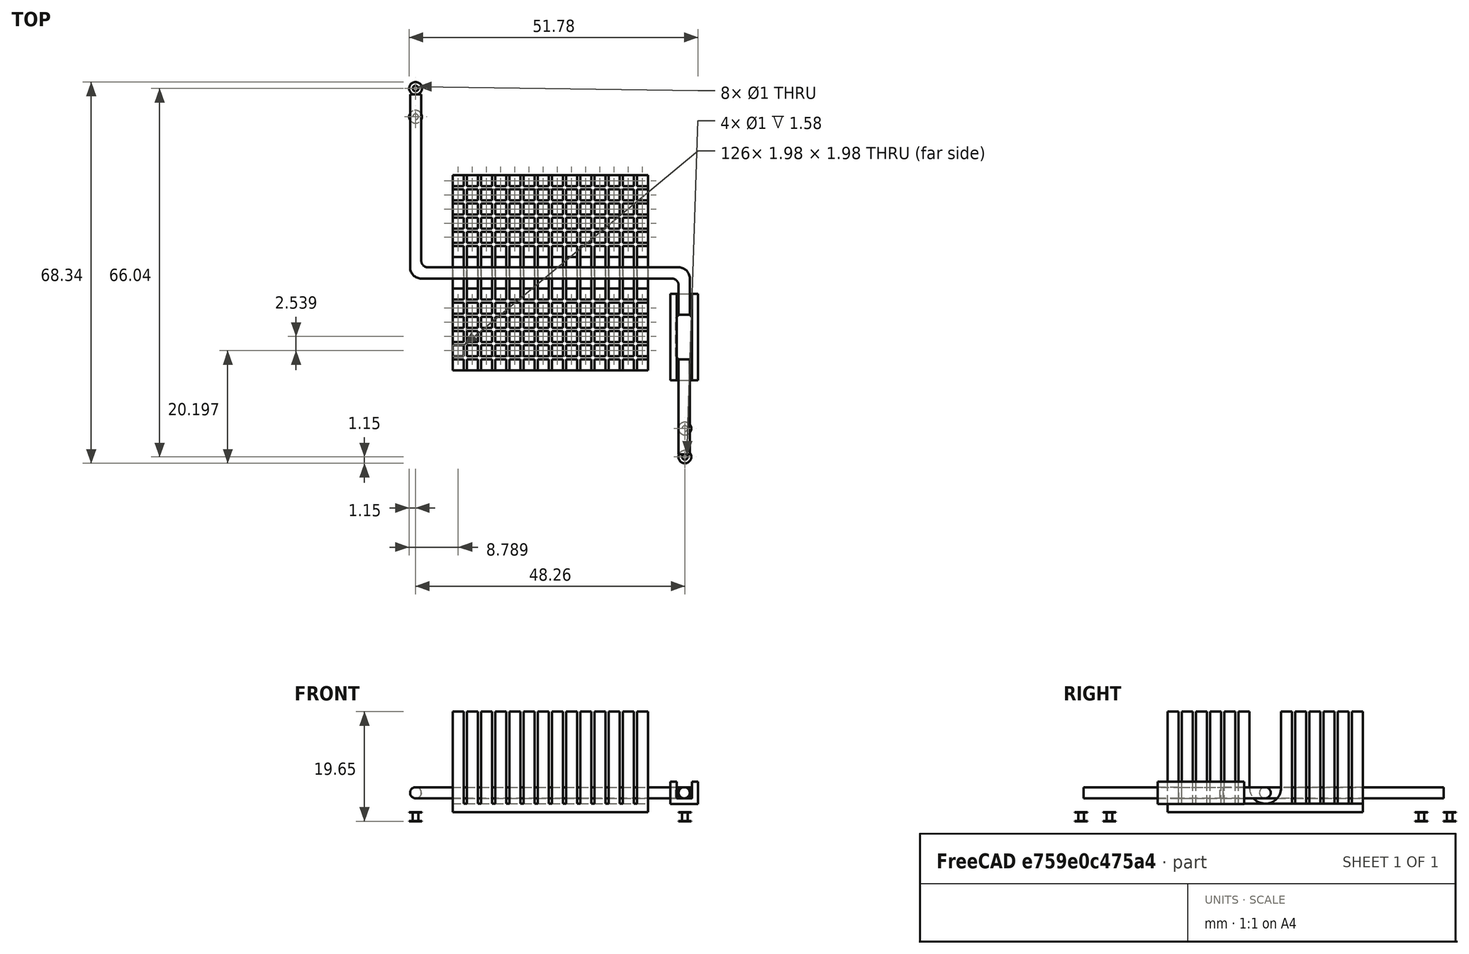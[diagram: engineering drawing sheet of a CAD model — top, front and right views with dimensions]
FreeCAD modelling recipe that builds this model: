
FCSTD DOCUMENT  (FreeCAD 0.20R29177 (Git))
Label: Aavid-heatsink3
License: All rights reserved
LicenseURL: http://en.wikipedia.org/wiki/All_rights_reserved
objects: PartDesign::AdditiveBox×7, PartDesign::Fillet×4, PartDesign::Body×4, Part::FeaturePython×3, Part::Feature×2, Sketcher::SketchObject×2, PartDesign::Chamfer×2, App::DocumentObjectGroup×1, PartDesign::SubtractiveBox×1, Part::Part2DObjectPython×1, PartDesign::Pad×1, App::Part×1
note: 41 computed .brp shape members not serialized (recipe doc carries the construction recipe); baked Part::Feature solids carry a one-line shape summary decoded from their .brp

FEATURE [Part::FeaturePython] FFab_lines  label="FFab"  # a2plus imported part (geometry in sourceFile) (typed FeaturePython)
  fixedPosition = true
FEATURE [Part::FeaturePython] THPs  label="PTHs"  # a2plus imported part (geometry in sourceFile) (typed FeaturePython)
  fixedPosition = true
FEATURE [Part::Feature] Shape001003  label="TopPads"
  shape: bbox 50.56 x 68.34 x 0.01 mm, 16 faces, 4 solids (baked)
FEATURE [Part::Feature] Shape001004  label="BotPads"
  shape: bbox 50.56 x 68.34 x 0.01 mm, 16 faces, 4 solids (baked)
FEATURE [App::DocumentObjectGroup] Heatsink_35x35mm_SpringFixation_fp
  Group = -> [FFab_lines,Shape001003,Shape001004,THPs]
FEATURE [Sketcher::SketchObject] Sketch  label="Pads_Poly"
  FullyConstrained = false
  MapMode = 5
  Support = -> [XY_Plane]
  sketch-geometry (56):
    g0: LineSegment StartX=-17.5 StartY=-17.45 StartZ=0 EndX=-17.5 EndY=17.55 EndZ=0
    g1: LineSegment StartX=-17.5 StartY=17.55 StartZ=0 EndX=-17.5 EndY=-17.55 EndZ=0
    g2: LineSegment StartX=-17.5 StartY=17.55 StartZ=0 EndX=17.55 EndY=17.5 EndZ=0
    g3: LineSegment StartX=17.55 StartY=17.5 StartZ=0 EndX=-17.5 EndY=17.45 EndZ=0
    g4: LineSegment StartX=17.55 StartY=17.5 StartZ=0 EndX=17.55 EndY=-17.5 EndZ=0
    g5: LineSegment StartX=17.5 StartY=-17.55 StartZ=0 EndX=17.45 EndY=17.5 EndZ=0
    g6: LineSegment StartX=17.5 StartY=-17.55 StartZ=0 EndX=-17.5 EndY=-17.55 EndZ=0
    g7: LineSegment StartX=-17.5 StartY=-17.45 StartZ=0 EndX=17.55 EndY=-17.5 EndZ=0
    g8: LineSegment StartX=-26.72 StartY=25.4 StartZ=0 EndX=-26.67 EndY=35.61 EndZ=0
    g9: LineSegment StartX=-26.67 StartY=35.61 StartZ=0 EndX=-26.62 EndY=25.4 EndZ=0
    g10: LineSegment StartX=-21.54 StartY=35.56 StartZ=0 EndX=-21.54 EndY=25.4 EndZ=0
    g11: LineSegment StartX=-21.64 StartY=25.4 StartZ=0 EndX=-21.64 EndY=35.56 EndZ=0
    g12: LineSegment StartX=-21.54 StartY=25.4 StartZ=0 EndX=-26.72 EndY=25.4 EndZ=0
    g13: LineSegment StartX=-26.72 StartY=25.4 StartZ=0 EndX=-21.54 EndY=25.4 EndZ=0
    g14: LineSegment StartX=-22.81 StartY=25.4 StartZ=0 EndX=-22.8271 EndY=2.54 EndZ=0
    g15: ArcOfCircle CenterX=-21.59 CenterY=2.55711 CenterZ=0 NormalX=0 NormalY=0 NormalZ=1 AngleXU=-1.5708 Radius=1.23726 StartAngle=4.72622 EndAngle=6.28319
    g16: LineSegment StartX=-21.59 StartY=1.31985 StartZ=0 EndX=-17.5 EndY=1.32 EndZ=0
    g17: LineSegment StartX=-17.5 StartY=1.22 StartZ=0 EndX=-21.59 EndY=1.29434 EndZ=0
    g18: ArcOfCircle CenterX=-21.5814 CenterY=2.54 CenterZ=0 NormalX=0 NormalY=0 NormalZ=1 AngleXU=-1.5708 Radius=1.24569 StartAngle=4.71239 EndAngle=6.27632
    g19: LineSegment StartX=-22.91 StartY=2.54 StartZ=0 EndX=-22.91 EndY=25.4 EndZ=0
    g20: LineSegment StartX=-25.35 StartY=1.27 StartZ=0 EndX=-25.45 EndY=25.4 EndZ=0
    g21: LineSegment StartX=-25.35 StartY=25.4 StartZ=0 EndX=-25.35 EndY=1.27 EndZ=0
    g22: ArcOfCircle CenterX=-22.86 CenterY=1.26185 CenterZ=0 NormalX=0 NormalY=0 NormalZ=1 AngleXU=-1.5708 Radius=2.49001 StartAngle=4.70911 EndAngle=6.28319
    g23: LineSegment StartX=-22.86 StartY=-1.22817 StartZ=0 EndX=-17.5 EndY=-1.22 EndZ=0
    g24: LineSegment StartX=-17.5 StartY=-1.32 StartZ=0 EndX=-22.86 EndY=-1.32 EndZ=0
    g25: ArcOfCircle CenterX=-22.86 CenterY=1.36352 CenterZ=0 NormalX=0 NormalY=0 NormalZ=1 AngleXU=-1.5708 Radius=2.59169 StartAngle=4.74848 EndAngle=6.28319
    g26: LineSegment StartX=-21.54 StartY=35.56 StartZ=0 EndX=-26.67 EndY=35.61 EndZ=0
    g27: LineSegment StartX=-26.67 StartY=35.61 StartZ=0 EndX=-21.54 EndY=35.56 EndZ=0
    g28: LineSegment StartX=21.59 StartY=-35.51 StartZ=0 EndX=21.59 EndY=-25.25 EndZ=0
    g29: LineSegment StartX=21.59 StartY=-25.25 StartZ=0 EndX=21.59 EndY=-35.51 EndZ=0
    g30: LineSegment StartX=26.67 StartY=-25.25 StartZ=0 EndX=26.72 EndY=-35.46 EndZ=0
    g31: LineSegment StartX=26.62 StartY=-35.46 StartZ=0 EndX=26.67 EndY=-25.25 EndZ=0
    g32: LineSegment StartX=21.59 StartY=-25.25 StartZ=0 EndX=26.67 EndY=-25.25 EndZ=0
    g33: LineSegment StartX=26.67 StartY=-25.35 StartZ=0 EndX=21.59 EndY=-25.35 EndZ=0
    g34: LineSegment StartX=25.35 StartY=-25.3 StartZ=0 EndX=25.35 EndY=-1.17 EndZ=0
    g35: ArcOfCircle CenterX=22.797 CenterY=-1.16077 CenterZ=0 NormalX=0 NormalY=0 NormalZ=1 AngleXU=1.5708 Radius=2.57229 StartAngle=4.7088 EndAngle=6.25869
    g36: LineSegment StartX=22.86 StartY=1.32 StartZ=0 EndX=17.5 EndY=1.32 EndZ=0
    g37: LineSegment StartX=17.5 StartY=1.42 StartZ=0 EndX=22.86 EndY=1.41075 EndZ=0
    g38: ArcOfCircle CenterX=22.86 CenterY=-1.17 CenterZ=0 NormalX=0 NormalY=0 NormalZ=1 AngleXU=1.5708 Radius=2.58075 StartAngle=4.71239 EndAngle=6.28319
    g39: LineSegment StartX=25.4407 StartY=-1.17 StartZ=0 EndX=25.45 EndY=-25.3 EndZ=0
    g40: LineSegment StartX=21.59 StartY=-35.51 StartZ=0 EndX=26.72 EndY=-35.46 EndZ=0
    g41: LineSegment StartX=26.72 StartY=-35.46 StartZ=0 EndX=21.59 EndY=-35.51 EndZ=0
    g42: LineSegment StartX=22.81 StartY=-2.44 StartZ=0 EndX=22.91 EndY=-25.3 EndZ=0
    g43: LineSegment StartX=22.81 StartY=-25.3 StartZ=0 EndX=22.81 EndY=-2.44 EndZ=0
    g44: ArcOfCircle CenterX=21.59 CenterY=-2.35008 CenterZ=0 NormalX=0 NormalY=0 NormalZ=1 AngleXU=1.5708 Radius=1.22331 StartAngle=4.63882 EndAngle=6.28319
    g45: LineSegment StartX=21.59 StartY=-1.12677 StartZ=0 EndX=17.5 EndY=-1.22 EndZ=0
    g46: LineSegment StartX=17.5 StartY=-1.12 StartZ=0 EndX=21.59 EndY=-1.12677 EndZ=0
    g47: ArcOfCircle CenterX=21.59 CenterY=-2.44679 CenterZ=0 NormalX=0 NormalY=0 NormalZ=1 AngleXU=1.5708 Radius=1.32002 StartAngle=4.71753 EndAngle=6.28319
    g48: LineSegment StartX=21.59 StartY=-18.525 StartZ=0 EndX=21.59 EndY=-3.125 EndZ=0
    g49: LineSegment StartX=21.59 StartY=-3.125 StartZ=0 EndX=21.59 EndY=-18.525 EndZ=0
    g50: LineSegment StartX=21.59 StartY=-18.525 StartZ=0 EndX=26.67 EndY=-18.525 EndZ=0
    g51: LineSegment StartX=26.67 StartY=-18.625 StartZ=0 EndX=21.59 EndY=-18.625 EndZ=0
    g52: LineSegment StartX=26.67 StartY=-18.525 StartZ=0 EndX=26.62 EndY=-3.075 EndZ=0
    g53: LineSegment StartX=26.72 StartY=-3.075 StartZ=0 EndX=26.67 EndY=-18.525 EndZ=0
    g54: LineSegment StartX=21.59 StartY=-3.125 StartZ=0 EndX=26.72 EndY=-3.075 EndZ=0
    g55: LineSegment StartX=26.72 StartY=-3.075 StartZ=0 EndX=21.59 EndY=-3.125 EndZ=0
  constraints (50):
    c: Coincident(g8,g12)
    c: Coincident(g8,g13)
    c: Coincident(g27,g8)
    c: Coincident(g27,g9)
    c: Coincident(g27,g26)
    c: Coincident(g22,g20)
    c: Coincident(g23,g25)
    c: Coincident(g23,g22)
    c: Coincident(g14,g15)
    c: Coincident(g14,g18)
    c: Coincident(g18,g17)
    c: Coincident(g15,g16)
    c: Coincident(g10,g12)
    c: Coincident(g10,g13)
    c: Coincident(g10,g26)
    c: Coincident(g10,g27)
    c: Coincident(g6,g1)
    c: Coincident(g7,g0)
    c: Coincident(g2,g0)
    c: Coincident(g2,g1)
    c: Coincident(g6,g5)
    c: Coincident(g4,g7)
    c: Coincident(g4,g3)
    c: Coincident(g4,g2)
    c: Coincident(g41,g28)
    c: Coincident(g41,g40)
    c: Coincident(g41,g29)
    c: Coincident(g32,g28)
    c: Coincident(g32,g29)
    c: Coincident(g50,g48)
    c: Coincident(g50,g49)
    c: Coincident(g55,g54)
    c: Coincident(g55,g48)
    c: Coincident(g55,g49)
    c: Coincident(g47,g45)
    c: Coincident(g47,g44)
    c: Coincident(g47,g46)
    c: Coincident(g44,g43)
    c: Coincident(g44,g42)
    c: Coincident(g37,g35)
    c: Coincident(g37,g38)
    c: Coincident(g39,g38)
    c: Coincident(g30,g40)
    c: Coincident(g30,g41)
    c: Coincident(g32,g31)
    c: Coincident(g32,g30)
    c: Coincident(g50,g52)
    c: Coincident(g50,g53)
    c: Coincident(g53,g54)
    c: Coincident(g53,g55)
FEATURE [PartDesign::AdditiveBox] Box  label="metal"
  AttacherType = Attacher::AttachEngine3D
  AttachmentOffset = pos=(-17.5,-17.5,0) rot=(0,0,1;0rad)
  Height = 1.5
  Length = 35
  MapMode = 5
  Placement = pos=(-17.5,-17.5,0) rot=(0,0,1;0rad)
  Support = -> [XY_Plane]
  Width = 35
FEATURE [PartDesign::AdditiveBox] Box010  label="base-lower-arm"
  AttacherType = Attacher::AttachEngine3D
  AttachmentOffset = pos=(23,-32,2.5) rot=(0,0,1;0rad)
  Height = 2
  Length = 2
  MapMode = 5
  Placement = pos=(23,-32,2.5) rot=(0,0,1;0rad)
  Support = -> [XY_Plane001]
  Width = 33.5
FEATURE [PartDesign::AdditiveBox] Box011  label="mid-arm"
  AttacherType = Attacher::AttachEngine3D
  AttachmentOffset = pos=(-23.1,-0.5,2.5) rot=(0,0,1;0rad)
  BaseFeature = -> Box010
  Height = 2
  Length = 46.1
  MapMode = 5
  Placement = pos=(-23.1,-0.5,2.5) rot=(0,0,1;0rad)
  Support = -> [XY_Plane001]
  Width = 2
FEATURE [PartDesign::AdditiveBox] Box012
  AttacherType = Attacher::AttachEngine3D
  AttachmentOffset = pos=(-25.1,-0.5,2.5) rot=(0,0,1;0rad)
  BaseFeature = -> Box011
  Height = 2
  Length = 2
  MapMode = 5
  Placement = pos=(-25.1,-0.5,2.5) rot=(0,0,1;0rad)
  Support = -> [XY_Plane001]
  Width = 33
FEATURE [PartDesign::Fillet] Fillet  label="outer-bend"
  Base = -> Box012 [Edge25,Edge19]
  BaseFeature = -> Box012
  Placement = pos=(-25.1,-0.5,2.5) rot=(0,0,1;0rad)
  Radius = 1.99
  SupportTransform = false
  UseAllEdges = false
FEATURE [PartDesign::Fillet] Fillet001  label="inner-bend"
  Base = -> Fillet [Edge17,Edge23]
  BaseFeature = -> Fillet
  Placement = pos=(-25.1,-0.5,2.5) rot=(0,0,1;0rad)
  Radius = 1.2
  SupportTransform = false
  UseAllEdges = false
FEATURE [PartDesign::Fillet] Fillet002  label="outer-smooth"
  Base = -> Fillet001 [Edge7,Edge5,Edge11,Edge12,Edge33,Edge20,Edge24,Edge29,Edge38,Edge25,Edge10,Edge50,Edge47,Edge43,Edge31,Edge1,Edge15,Edge16,Edge37,Edge35,Edge36]
  BaseFeature = -> Fillet001
  Placement = pos=(-25.1,-0.5,2.5) rot=(0,0,1;0rad)
  Radius = 0.99
  SupportTransform = false
  UseAllEdges = false
FEATURE [PartDesign::AdditiveBox] Box014
  AttacherType = Attacher::AttachEngine3D
  AttachmentOffset = pos=(21.5,-18.6,1.5) rot=(0,0,1;0rad)
  Height = 4
  Length = 5
  MapMode = 5
  Placement = pos=(21.5,-18.6,1.5) rot=(0,0,1;0rad)
  Support = -> [XY_Plane002]
  Width = 15.5
FEATURE [PartDesign::SubtractiveBox] Box015
  AttacherType = Attacher::AttachEngine3D
  AttachmentOffset = pos=(22.65,-19,2.5) rot=(0,0,1;0rad)
  BaseFeature = -> Box014
  Height = 3
  Length = 2.75
  MapMode = 5
  Placement = pos=(22.65,-19,2.5) rot=(0,0,1;0rad)
  Support = -> [XY_Plane002]
  Width = 16
FEATURE [PartDesign::AdditiveBox] Box016
  AttacherType = Attacher::AttachEngine3D
  AttachmentOffset = pos=(-15,-15,0) rot=(0,0,1;0rad)
  Height = 0.05
  Length = 30
  MapMode = 5
  Placement = pos=(-15,-15,0) rot=(0,0,1;0rad)
  Support = -> [XY_Plane004]
  Width = 30
FEATURE [Part::Part2DObjectPython] Shape2DView  # Draft 2D object (typed FeaturePython)
  AutoUpdate = true
  Clip = false
  FuseArch = false
  HiddenLines = false
  InPlace = true
  OnlySolids = false
  Projection = (0,0,1)
  ProjectionMode = 0
  SegmentLength = 0.05
  Tessellation = false
  VisibleOnly = false
FEATURE [Part::FeaturePython] Array  # Draft array (typed FeaturePython)
  AlwaysSyncPlacement = false
  Angle = 360
  ArrayType = 0
  Axis = (0,0,1)
  Base = -> Shape2DView
  Center = (0,0,0)
  Count = 196
  ExpandArray = false
  Fuse = false
  IntervalAxis = (0,0,0)
  IntervalX = (2.5387,0,0)
  IntervalY = (0,2.5387,0)
  IntervalZ = (0,0,100)
  NumberCircles = 3
  NumberPolar = 5
  NumberX = 14
  NumberY = 14
  NumberZ = 1
  Placement = pos=(0,-33.0245,0) rot=(0,0,1;0rad)
  PlacementList = 196 placements: [(0,0,0),(0,2.5387,0),(0,5.0774,0),(0,7.6161,0),(0,10.1548,0),(0,12.6935,0),(0,15.2322,0),(0,17.7709,0),(0,20.3096,0),(0,22.8483,0),(0,25.387,0),(0,27.9257,0),(0,30.4644,0),(0,33.0031,0),(2.5387,0,0),(2.5387,2.5387,0),(2.5387,5.0774,0),(2.5387,7.6161,0),(2.5387,10.1548,0),(2.5387,12.6935,0),(2.5387,15.2322,0),(2.5387,17.7709,0),(2.5387,20.3096,0),(2.5387,22.8483,0),(2.5387,25.387,0),+171 more]
  RadialDistance = 50
  ScaleList = (196) [(1,1,1),(1,1,1),(1,1,1),(1,1,1),(1,1,1),(1,1,1),(1,1,1),(1,1,1),(1,1,1),(1,1,1),(1,1,1),(1,1,1),(1,1,1),(1,1,1),(1,1,1),(1,1,1),(1,1,1),(1,1,1),+178 more]
  Symmetry = 1
  TangentialDistance = 25
FEATURE [Sketcher::SketchObject] Sketch001  label="fin-sketch"
  FullyConstrained = false
  sketch-geometry (672):
    g0: LineSegment StartX=-17.5 StartY=-17.5 StartZ=0 EndX=-17.5 EndY=-15.5245 EndZ=0
    g1: LineSegment StartX=-15.5245 StartY=-17.5 StartZ=0 EndX=-15.5245 EndY=-15.5245 EndZ=0
    g2: LineSegment StartX=-17.5 StartY=-17.5 StartZ=0 EndX=-15.5245 EndY=-17.5 EndZ=0
    g3: LineSegment StartX=-17.5 StartY=-15.5245 StartZ=0 EndX=-15.5245 EndY=-15.5245 EndZ=0
    g4: LineSegment StartX=-17.5 StartY=-14.9613 StartZ=0 EndX=-17.5 EndY=-12.9858 EndZ=0
    g5: LineSegment StartX=-15.5245 StartY=-14.9613 StartZ=0 EndX=-15.5245 EndY=-12.9858 EndZ=0
    g6: LineSegment StartX=-17.5 StartY=-14.9613 StartZ=0 EndX=-15.5245 EndY=-14.9613 EndZ=0
    g7: LineSegment StartX=-17.5 StartY=-12.9858 StartZ=0 EndX=-15.5245 EndY=-12.9858 EndZ=0
    g8: LineSegment StartX=-17.5 StartY=-12.4226 StartZ=0 EndX=-17.5 EndY=-10.4471 EndZ=0
    g9: LineSegment StartX=-15.5245 StartY=-12.4226 StartZ=0 EndX=-15.5245 EndY=-10.4471 EndZ=0
    g10: LineSegment StartX=-17.5 StartY=-12.4226 StartZ=0 EndX=-15.5245 EndY=-12.4226 EndZ=0
    g11: LineSegment StartX=-17.5 StartY=-10.4471 StartZ=0 EndX=-15.5245 EndY=-10.4471 EndZ=0
    g12: LineSegment StartX=-17.5 StartY=-9.88385 StartZ=0 EndX=-17.5 EndY=-7.90835 EndZ=0
    g13: LineSegment StartX=-15.5245 StartY=-9.88385 StartZ=0 EndX=-15.5245 EndY=-7.90835 EndZ=0
    g14: LineSegment StartX=-17.5 StartY=-9.88385 StartZ=0 EndX=-15.5245 EndY=-9.88385 EndZ=0
    g15: LineSegment StartX=-17.5 StartY=-7.90835 StartZ=0 EndX=-15.5245 EndY=-7.90835 EndZ=0
    g16: LineSegment StartX=-17.5 StartY=-7.34515 StartZ=0 EndX=-17.5 EndY=-5.36965 EndZ=0
    g17: LineSegment StartX=-15.5245 StartY=-7.34515 StartZ=0 EndX=-15.5245 EndY=-5.36965 EndZ=0
    g18: LineSegment StartX=-17.5 StartY=-7.34515 StartZ=0 EndX=-15.5245 EndY=-7.34515 EndZ=0
    g19: LineSegment StartX=-17.5 StartY=-5.36965 StartZ=0 EndX=-15.5245 EndY=-5.36965 EndZ=0
    g20: LineSegment StartX=-17.5 StartY=-4.80645 StartZ=0 EndX=-17.5 EndY=-2.83095 EndZ=0
    g21: LineSegment StartX=-15.5245 StartY=-4.80645 StartZ=0 EndX=-15.5245 EndY=-2.83095 EndZ=0
    g22: LineSegment StartX=-17.5 StartY=-4.80645 StartZ=0 EndX=-15.5245 EndY=-4.80645 EndZ=0
    g23: LineSegment StartX=-17.5 StartY=-2.83095 StartZ=0 EndX=-15.5245 EndY=-2.83095 EndZ=0
    g24: LineSegment StartX=-17.5 StartY=-2.26775 StartZ=0 EndX=-17.5 EndY=-0.292254 EndZ=0
    g25: LineSegment StartX=-15.5245 StartY=-2.26775 StartZ=0 EndX=-15.5245 EndY=-0.292254 EndZ=0
    g26: LineSegment StartX=-17.5 StartY=-2.26775 StartZ=0 EndX=-15.5245 EndY=-2.26775 EndZ=0
    g27: LineSegment StartX=-17.5 StartY=-0.292254 StartZ=0 EndX=-15.5245 EndY=-0.292254 EndZ=0
    g28: LineSegment StartX=-17.5 StartY=0.270946 StartZ=0 EndX=-17.5 EndY=2.24645 EndZ=0
    g29: LineSegment StartX=-15.5245 StartY=0.270946 StartZ=0 EndX=-15.5245 EndY=2.24645 EndZ=0
    g30: LineSegment StartX=-17.5 StartY=0.270946 StartZ=0 EndX=-15.5245 EndY=0.270946 EndZ=0
    g31: LineSegment StartX=-17.5 StartY=2.24645 StartZ=0 EndX=-15.5245 EndY=2.24645 EndZ=0
    g32: LineSegment StartX=-17.5 StartY=2.80965 StartZ=0 EndX=-17.5 EndY=4.78515 EndZ=0
    g33: LineSegment StartX=-15.5245 StartY=2.80965 StartZ=0 EndX=-15.5245 EndY=4.78515 EndZ=0
    g34: LineSegment StartX=-17.5 StartY=2.80965 StartZ=0 EndX=-15.5245 EndY=2.80965 EndZ=0
    g35: LineSegment StartX=-17.5 StartY=4.78515 StartZ=0 EndX=-15.5245 EndY=4.78515 EndZ=0
    g36: LineSegment StartX=-17.5 StartY=5.34835 StartZ=0 EndX=-17.5 EndY=7.32385 EndZ=0
    g37: LineSegment StartX=-15.5245 StartY=5.34835 StartZ=0 EndX=-15.5245 EndY=7.32385 EndZ=0
    g38: LineSegment StartX=-17.5 StartY=5.34835 StartZ=0 EndX=-15.5245 EndY=5.34835 EndZ=0
    g39: LineSegment StartX=-17.5 StartY=7.32385 StartZ=0 EndX=-15.5245 EndY=7.32385 EndZ=0
    g40: LineSegment StartX=-17.5 StartY=7.88705 StartZ=0 EndX=-17.5 EndY=9.86255 EndZ=0
    g41: LineSegment StartX=-15.5245 StartY=7.88705 StartZ=0 EndX=-15.5245 EndY=9.86255 EndZ=0
    g42: LineSegment StartX=-17.5 StartY=7.88705 StartZ=0 EndX=-15.5245 EndY=7.88705 EndZ=0
    g43: LineSegment StartX=-17.5 StartY=9.86255 StartZ=0 EndX=-15.5245 EndY=9.86255 EndZ=0
    g44: LineSegment StartX=-17.5 StartY=10.4257 StartZ=0 EndX=-17.5 EndY=12.4012 EndZ=0
    g45: LineSegment StartX=-15.5245 StartY=10.4257 StartZ=0 EndX=-15.5245 EndY=12.4012 EndZ=0
    g46: LineSegment StartX=-17.5 StartY=10.4257 StartZ=0 EndX=-15.5245 EndY=10.4257 EndZ=0
    g47: LineSegment StartX=-17.5 StartY=12.4012 StartZ=0 EndX=-15.5245 EndY=12.4012 EndZ=0
    g48: LineSegment StartX=-17.5 StartY=12.9644 StartZ=0 EndX=-17.5 EndY=14.9399 EndZ=0
    g49: LineSegment StartX=-15.5245 StartY=12.9644 StartZ=0 EndX=-15.5245 EndY=14.9399 EndZ=0
    g50: LineSegment StartX=-17.5 StartY=12.9644 StartZ=0 EndX=-15.5245 EndY=12.9644 EndZ=0
    g51: LineSegment StartX=-17.5 StartY=14.9399 StartZ=0 EndX=-15.5245 EndY=14.9399 EndZ=0
    g52: LineSegment StartX=-17.5 StartY=15.5031 StartZ=0 EndX=-17.5 EndY=17.4786 EndZ=0
    g53: LineSegment StartX=-15.5245 StartY=15.5031 StartZ=0 EndX=-15.5245 EndY=17.4786 EndZ=0
    g54: LineSegment StartX=-17.5 StartY=15.5031 StartZ=0 EndX=-15.5245 EndY=15.5031 EndZ=0
    g55: LineSegment StartX=-17.5 StartY=17.4786 StartZ=0 EndX=-15.5245 EndY=17.4786 EndZ=0
    g56: LineSegment StartX=-14.9613 StartY=-17.5 StartZ=0 EndX=-14.9613 EndY=-15.5245 EndZ=0
    g57: LineSegment StartX=-12.9858 StartY=-17.5 StartZ=0 EndX=-12.9858 EndY=-15.5245 EndZ=0
    g58: LineSegment StartX=-14.9613 StartY=-17.5 StartZ=0 EndX=-12.9858 EndY=-17.5 EndZ=0
    g59: LineSegment StartX=-14.9613 StartY=-15.5245 StartZ=0 EndX=-12.9858 EndY=-15.5245 EndZ=0
    g60: LineSegment StartX=-14.9613 StartY=-14.9613 StartZ=0 EndX=-14.9613 EndY=-12.9858 EndZ=0
    g61: LineSegment StartX=-12.9858 StartY=-14.9613 StartZ=0 EndX=-12.9858 EndY=-12.9858 EndZ=0
    g62: LineSegment StartX=-14.9613 StartY=-14.9613 StartZ=0 EndX=-12.9858 EndY=-14.9613 EndZ=0
    g63: LineSegment StartX=-14.9613 StartY=-12.9858 StartZ=0 EndX=-12.9858 EndY=-12.9858 EndZ=0
    g64: LineSegment StartX=-14.9613 StartY=-12.4226 StartZ=0 EndX=-14.9613 EndY=-10.4471 EndZ=0
    g65: LineSegment StartX=-12.9858 StartY=-12.4226 StartZ=0 EndX=-12.9858 EndY=-10.4471 EndZ=0
    g66: LineSegment StartX=-14.9613 StartY=-12.4226 StartZ=0 EndX=-12.9858 EndY=-12.4226 EndZ=0
    g67: LineSegment StartX=-14.9613 StartY=-10.4471 StartZ=0 EndX=-12.9858 EndY=-10.4471 EndZ=0
    g68: LineSegment StartX=-14.9613 StartY=-9.88385 StartZ=0 EndX=-14.9613 EndY=-7.90835 EndZ=0
    g69: LineSegment StartX=-12.9858 StartY=-9.88385 StartZ=0 EndX=-12.9858 EndY=-7.90835 EndZ=0
    g70: LineSegment StartX=-14.9613 StartY=-9.88385 StartZ=0 EndX=-12.9858 EndY=-9.88385 EndZ=0
    g71: LineSegment StartX=-14.9613 StartY=-7.90835 StartZ=0 EndX=-12.9858 EndY=-7.90835 EndZ=0
    g72: LineSegment StartX=-14.9613 StartY=-7.34515 StartZ=0 EndX=-14.9613 EndY=-5.36965 EndZ=0
    g73: LineSegment StartX=-12.9858 StartY=-7.34515 StartZ=0 EndX=-12.9858 EndY=-5.36965 EndZ=0
    g74: LineSegment StartX=-14.9613 StartY=-7.34515 StartZ=0 EndX=-12.9858 EndY=-7.34515 EndZ=0
    g75: LineSegment StartX=-14.9613 StartY=-5.36965 StartZ=0 EndX=-12.9858 EndY=-5.36965 EndZ=0
    g76: LineSegment StartX=-14.9613 StartY=-4.80645 StartZ=0 EndX=-14.9613 EndY=-2.83095 EndZ=0
    g77: LineSegment StartX=-12.9858 StartY=-4.80645 StartZ=0 EndX=-12.9858 EndY=-2.83095 EndZ=0
    g78: LineSegment StartX=-14.9613 StartY=-4.80645 StartZ=0 EndX=-12.9858 EndY=-4.80645 EndZ=0
    g79: LineSegment StartX=-14.9613 StartY=-2.83095 StartZ=0 EndX=-12.9858 EndY=-2.83095 EndZ=0
    g80: LineSegment StartX=-14.9613 StartY=-2.26775 StartZ=0 EndX=-14.9613 EndY=-0.292254 EndZ=0
    g81: LineSegment StartX=-12.9858 StartY=-2.26775 StartZ=0 EndX=-12.9858 EndY=-0.292254 EndZ=0
    g82: LineSegment StartX=-14.9613 StartY=-2.26775 StartZ=0 EndX=-12.9858 EndY=-2.26775 EndZ=0
    g83: LineSegment StartX=-14.9613 StartY=-0.292254 StartZ=0 EndX=-12.9858 EndY=-0.292254 EndZ=0
    g84: LineSegment StartX=-14.9613 StartY=0.270946 StartZ=0 EndX=-14.9613 EndY=2.24645 EndZ=0
    g85: LineSegment StartX=-12.9858 StartY=0.270946 StartZ=0 EndX=-12.9858 EndY=2.24645 EndZ=0
    g86: LineSegment StartX=-14.9613 StartY=0.270946 StartZ=0 EndX=-12.9858 EndY=0.270946 EndZ=0
    g87: LineSegment StartX=-14.9613 StartY=2.24645 StartZ=0 EndX=-12.9858 EndY=2.24645 EndZ=0
    g88: LineSegment StartX=-14.9613 StartY=2.80965 StartZ=0 EndX=-14.9613 EndY=4.78515 EndZ=0
    g89: LineSegment StartX=-12.9858 StartY=2.80965 StartZ=0 EndX=-12.9858 EndY=4.78515 EndZ=0
    g90: LineSegment StartX=-14.9613 StartY=2.80965 StartZ=0 EndX=-12.9858 EndY=2.80965 EndZ=0
    g91: LineSegment StartX=-14.9613 StartY=4.78515 StartZ=0 EndX=-12.9858 EndY=4.78515 EndZ=0
    g92: LineSegment StartX=-14.9613 StartY=5.34835 StartZ=0 EndX=-14.9613 EndY=7.32385 EndZ=0
    g93: LineSegment StartX=-12.9858 StartY=5.34835 StartZ=0 EndX=-12.9858 EndY=7.32385 EndZ=0
    g94: LineSegment StartX=-14.9613 StartY=5.34835 StartZ=0 EndX=-12.9858 EndY=5.34835 EndZ=0
    g95: LineSegment StartX=-14.9613 StartY=7.32385 StartZ=0 EndX=-12.9858 EndY=7.32385 EndZ=0
    g96: LineSegment StartX=-14.9613 StartY=7.88705 StartZ=0 EndX=-14.9613 EndY=9.86255 EndZ=0
    g97: LineSegment StartX=-12.9858 StartY=7.88705 StartZ=0 EndX=-12.9858 EndY=9.86255 EndZ=0
    g98: LineSegment StartX=-14.9613 StartY=7.88705 StartZ=0 EndX=-12.9858 EndY=7.88705 EndZ=0
    g99: LineSegment StartX=-14.9613 StartY=9.86255 StartZ=0 EndX=-12.9858 EndY=9.86255 EndZ=0
    g100: LineSegment StartX=-14.9613 StartY=10.4257 StartZ=0 EndX=-14.9613 EndY=12.4012 EndZ=0
    g101: LineSegment StartX=-12.9858 StartY=10.4257 StartZ=0 EndX=-12.9858 EndY=12.4012 EndZ=0
    g102: LineSegment StartX=-14.9613 StartY=10.4257 StartZ=0 EndX=-12.9858 EndY=10.4257 EndZ=0
    g103: LineSegment StartX=-14.9613 StartY=12.4012 StartZ=0 EndX=-12.9858 EndY=12.4012 EndZ=0
    g104: LineSegment StartX=-14.9613 StartY=12.9644 StartZ=0 EndX=-14.9613 EndY=14.9399 EndZ=0
    g105: LineSegment StartX=-12.9858 StartY=12.9644 StartZ=0 EndX=-12.9858 EndY=14.9399 EndZ=0
    g106: LineSegment StartX=-14.9613 StartY=12.9644 StartZ=0 EndX=-12.9858 EndY=12.9644 EndZ=0
    g107: LineSegment StartX=-14.9613 StartY=14.9399 StartZ=0 EndX=-12.9858 EndY=14.9399 EndZ=0
    g108: LineSegment StartX=-14.9613 StartY=15.5031 StartZ=0 EndX=-14.9613 EndY=17.4786 EndZ=0
    g109: LineSegment StartX=-12.9858 StartY=15.5031 StartZ=0 EndX=-12.9858 EndY=17.4786 EndZ=0
    g110: LineSegment StartX=-14.9613 StartY=15.5031 StartZ=0 EndX=-12.9858 EndY=15.5031 EndZ=0
    g111: LineSegment StartX=-14.9613 StartY=17.4786 StartZ=0 EndX=-12.9858 EndY=17.4786 EndZ=0
    g112: LineSegment StartX=-12.4226 StartY=-17.5 StartZ=0 EndX=-12.4226 EndY=-15.5245 EndZ=0
    g113: LineSegment StartX=-10.4471 StartY=-17.5 StartZ=0 EndX=-10.4471 EndY=-15.5245 EndZ=0
    g114: LineSegment StartX=-12.4226 StartY=-17.5 StartZ=0 EndX=-10.4471 EndY=-17.5 EndZ=0
    g115: LineSegment StartX=-12.4226 StartY=-15.5245 StartZ=0 EndX=-10.4471 EndY=-15.5245 EndZ=0
    g116: LineSegment StartX=-12.4226 StartY=-14.9613 StartZ=0 EndX=-12.4226 EndY=-12.9858 EndZ=0
    g117: LineSegment StartX=-10.4471 StartY=-14.9613 StartZ=0 EndX=-10.4471 EndY=-12.9858 EndZ=0
    g118: LineSegment StartX=-12.4226 StartY=-14.9613 StartZ=0 EndX=-10.4471 EndY=-14.9613 EndZ=0
    g119: LineSegment StartX=-12.4226 StartY=-12.9858 StartZ=0 EndX=-10.4471 EndY=-12.9858 EndZ=0
    g120: LineSegment StartX=-12.4226 StartY=-12.4226 StartZ=0 EndX=-12.4226 EndY=-10.4471 EndZ=0
    g121: LineSegment StartX=-10.4471 StartY=-12.4226 StartZ=0 EndX=-10.4471 EndY=-10.4471 EndZ=0
    g122: LineSegment StartX=-12.4226 StartY=-12.4226 StartZ=0 EndX=-10.4471 EndY=-12.4226 EndZ=0
    g123: LineSegment StartX=-12.4226 StartY=-10.4471 StartZ=0 EndX=-10.4471 EndY=-10.4471 EndZ=0
    g124: LineSegment StartX=-12.4226 StartY=-9.88385 StartZ=0 EndX=-12.4226 EndY=-7.90835 EndZ=0
    g125: LineSegment StartX=-10.4471 StartY=-9.88385 StartZ=0 EndX=-10.4471 EndY=-7.90835 EndZ=0
    g126: LineSegment StartX=-12.4226 StartY=-9.88385 StartZ=0 EndX=-10.4471 EndY=-9.88385 EndZ=0
    g127: LineSegment StartX=-12.4226 StartY=-7.90835 StartZ=0 EndX=-10.4471 EndY=-7.90835 EndZ=0
    g128: LineSegment StartX=-12.4226 StartY=-7.34515 StartZ=0 EndX=-12.4226 EndY=-5.36965 EndZ=0
    g129: LineSegment StartX=-10.4471 StartY=-7.34515 StartZ=0 EndX=-10.4471 EndY=-5.36965 EndZ=0
    g130: LineSegment StartX=-12.4226 StartY=-7.34515 StartZ=0 EndX=-10.4471 EndY=-7.34515 EndZ=0
    g131: LineSegment StartX=-12.4226 StartY=-5.36965 StartZ=0 EndX=-10.4471 EndY=-5.36965 EndZ=0
    g132: LineSegment StartX=-12.4226 StartY=-4.80645 StartZ=0 EndX=-12.4226 EndY=-2.83095 EndZ=0
    g133: LineSegment StartX=-10.4471 StartY=-4.80645 StartZ=0 EndX=-10.4471 EndY=-2.83095 EndZ=0
    g134: LineSegment StartX=-12.4226 StartY=-4.80645 StartZ=0 EndX=-10.4471 EndY=-4.80645 EndZ=0
    g135: LineSegment StartX=-12.4226 StartY=-2.83095 StartZ=0 EndX=-10.4471 EndY=-2.83095 EndZ=0
    g136: LineSegment StartX=-12.4226 StartY=-2.26775 StartZ=0 EndX=-12.4226 EndY=-0.292254 EndZ=0
    g137: LineSegment StartX=-10.4471 StartY=-2.26775 StartZ=0 EndX=-10.4471 EndY=-0.292254 EndZ=0
    g138: LineSegment StartX=-12.4226 StartY=-2.26775 StartZ=0 EndX=-10.4471 EndY=-2.26775 EndZ=0
    g139: LineSegment StartX=-12.4226 StartY=-0.292254 StartZ=0 EndX=-10.4471 EndY=-0.292254 EndZ=0
    g140: LineSegment StartX=-12.4226 StartY=0.270946 StartZ=0 EndX=-12.4226 EndY=2.24645 EndZ=0
    g141: LineSegment StartX=-10.4471 StartY=0.270946 StartZ=0 EndX=-10.4471 EndY=2.24645 EndZ=0
    g142: LineSegment StartX=-12.4226 StartY=0.270946 StartZ=0 EndX=-10.4471 EndY=0.270946 EndZ=0
    g143: LineSegment StartX=-12.4226 StartY=2.24645 StartZ=0 EndX=-10.4471 EndY=2.24645 EndZ=0
    g144: LineSegment StartX=-12.4226 StartY=2.80965 StartZ=0 EndX=-12.4226 EndY=4.78515 EndZ=0
    g145: LineSegment StartX=-10.4471 StartY=2.80965 StartZ=0 EndX=-10.4471 EndY=4.78515 EndZ=0
    g146: LineSegment StartX=-12.4226 StartY=2.80965 StartZ=0 EndX=-10.4471 EndY=2.80965 EndZ=0
    g147: LineSegment StartX=-12.4226 StartY=4.78515 StartZ=0 EndX=-10.4471 EndY=4.78515 EndZ=0
    g148: LineSegment StartX=-12.4226 StartY=5.34835 StartZ=0 EndX=-12.4226 EndY=7.32385 EndZ=0
    g149: LineSegment StartX=-10.4471 StartY=5.34835 StartZ=0 EndX=-10.4471 EndY=7.32385 EndZ=0
    g150: LineSegment StartX=-12.4226 StartY=5.34835 StartZ=0 EndX=-10.4471 EndY=5.34835 EndZ=0
    g151: LineSegment StartX=-12.4226 StartY=7.32385 StartZ=0 EndX=-10.4471 EndY=7.32385 EndZ=0
    g152: LineSegment StartX=-12.4226 StartY=7.88705 StartZ=0 EndX=-12.4226 EndY=9.86255 EndZ=0
    g153: LineSegment StartX=-10.4471 StartY=7.88705 StartZ=0 EndX=-10.4471 EndY=9.86255 EndZ=0
    g154: LineSegment StartX=-12.4226 StartY=7.88705 StartZ=0 EndX=-10.4471 EndY=7.88705 EndZ=0
    g155: LineSegment StartX=-12.4226 StartY=9.86255 StartZ=0 EndX=-10.4471 EndY=9.86255 EndZ=0
    g156: LineSegment StartX=-12.4226 StartY=10.4257 StartZ=0 EndX=-12.4226 EndY=12.4012 EndZ=0
    g157: LineSegment StartX=-10.4471 StartY=10.4257 StartZ=0 EndX=-10.4471 EndY=12.4012 EndZ=0
    g158: LineSegment StartX=-12.4226 StartY=10.4257 StartZ=0 EndX=-10.4471 EndY=10.4257 EndZ=0
    g159: LineSegment StartX=-12.4226 StartY=12.4012 StartZ=0 EndX=-10.4471 EndY=12.4012 EndZ=0
    g160: LineSegment StartX=-12.4226 StartY=12.9644 StartZ=0 EndX=-12.4226 EndY=14.9399 EndZ=0
    g161: LineSegment StartX=-10.4471 StartY=12.9644 StartZ=0 EndX=-10.4471 EndY=14.9399 EndZ=0
    g162: LineSegment StartX=-12.4226 StartY=12.9644 StartZ=0 EndX=-10.4471 EndY=12.9644 EndZ=0
    g163: LineSegment StartX=-12.4226 StartY=14.9399 StartZ=0 EndX=-10.4471 EndY=14.9399 EndZ=0
    g164: LineSegment StartX=-12.4226 StartY=15.5031 StartZ=0 EndX=-12.4226 EndY=17.4786 EndZ=0
    g165: LineSegment StartX=-10.4471 StartY=15.5031 StartZ=0 EndX=-10.4471 EndY=17.4786 EndZ=0
    g166: LineSegment StartX=-12.4226 StartY=15.5031 StartZ=0 EndX=-10.4471 EndY=15.5031 EndZ=0
    g167: LineSegment StartX=-12.4226 StartY=17.4786 StartZ=0 EndX=-10.4471 EndY=17.4786 EndZ=0
    g168: LineSegment StartX=-9.8839 StartY=-17.5 StartZ=0 EndX=-9.8839 EndY=-15.5245 EndZ=0
    g169: LineSegment StartX=-7.9084 StartY=-17.5 StartZ=0 EndX=-7.9084 EndY=-15.5245 EndZ=0
    g170: LineSegment StartX=-9.8839 StartY=-17.5 StartZ=0 EndX=-7.9084 EndY=-17.5 EndZ=0
    g171: LineSegment StartX=-9.8839 StartY=-15.5245 StartZ=0 EndX=-7.9084 EndY=-15.5245 EndZ=0
    g172: LineSegment StartX=-9.8839 StartY=-14.9613 StartZ=0 EndX=-9.8839 EndY=-12.9858 EndZ=0
    g173: LineSegment StartX=-7.9084 StartY=-14.9613 StartZ=0 EndX=-7.9084 EndY=-12.9858 EndZ=0
    g174: LineSegment StartX=-9.8839 StartY=-14.9613 StartZ=0 EndX=-7.9084 EndY=-14.9613 EndZ=0
    g175: LineSegment StartX=-9.8839 StartY=-12.9858 StartZ=0 EndX=-7.9084 EndY=-12.9858 EndZ=0
    g176: LineSegment StartX=-9.8839 StartY=-12.4226 StartZ=0 EndX=-9.8839 EndY=-10.4471 EndZ=0
    g177: LineSegment StartX=-7.9084 StartY=-12.4226 StartZ=0 EndX=-7.9084 EndY=-10.4471 EndZ=0
    g178: LineSegment StartX=-9.8839 StartY=-12.4226 StartZ=0 EndX=-7.9084 EndY=-12.4226 EndZ=0
    g179: LineSegment StartX=-9.8839 StartY=-10.4471 StartZ=0 EndX=-7.9084 EndY=-10.4471 EndZ=0
    g180: LineSegment StartX=-9.8839 StartY=-9.88385 StartZ=0 EndX=-9.8839 EndY=-7.90835 EndZ=0
    g181: LineSegment StartX=-7.9084 StartY=-9.88385 StartZ=0 EndX=-7.9084 EndY=-7.90835 EndZ=0
    g182: LineSegment StartX=-9.8839 StartY=-9.88385 StartZ=0 EndX=-7.9084 EndY=-9.88385 EndZ=0
    g183: LineSegment StartX=-9.8839 StartY=-7.90835 StartZ=0 EndX=-7.9084 EndY=-7.90835 EndZ=0
    g184: LineSegment StartX=-9.8839 StartY=-7.34515 StartZ=0 EndX=-9.8839 EndY=-5.36965 EndZ=0
    g185: LineSegment StartX=-7.9084 StartY=-7.34515 StartZ=0 EndX=-7.9084 EndY=-5.36965 EndZ=0
    g186: LineSegment StartX=-9.8839 StartY=-7.34515 StartZ=0 EndX=-7.9084 EndY=-7.34515 EndZ=0
    g187: LineSegment StartX=-9.8839 StartY=-5.36965 StartZ=0 EndX=-7.9084 EndY=-5.36965 EndZ=0
    g188: LineSegment StartX=-9.8839 StartY=-4.80645 StartZ=0 EndX=-9.8839 EndY=-2.83095 EndZ=0
    g189: LineSegment StartX=-7.9084 StartY=-4.80645 StartZ=0 EndX=-7.9084 EndY=-2.83095 EndZ=0
    g190: LineSegment StartX=-9.8839 StartY=-4.80645 StartZ=0 EndX=-7.9084 EndY=-4.80645 EndZ=0
    g191: LineSegment StartX=-9.8839 StartY=-2.83095 StartZ=0 EndX=-7.9084 EndY=-2.83095 EndZ=0
    g192: LineSegment StartX=-9.8839 StartY=-2.26775 StartZ=0 EndX=-9.8839 EndY=-0.292254 EndZ=0
    g193: LineSegment StartX=-7.9084 StartY=-2.26775 StartZ=0 EndX=-7.9084 EndY=-0.292254 EndZ=0
    g194: LineSegment StartX=-9.8839 StartY=-2.26775 StartZ=0 EndX=-7.9084 EndY=-2.26775 EndZ=0
    g195: LineSegment StartX=-9.8839 StartY=-0.292254 StartZ=0 EndX=-7.9084 EndY=-0.292254 EndZ=0
    g196: LineSegment StartX=-9.8839 StartY=0.270946 StartZ=0 EndX=-9.8839 EndY=2.24645 EndZ=0
    g197: LineSegment StartX=-7.9084 StartY=0.270946 StartZ=0 EndX=-7.9084 EndY=2.24645 EndZ=0
    g198: LineSegment StartX=-9.8839 StartY=0.270946 StartZ=0 EndX=-7.9084 EndY=0.270946 EndZ=0
    g199: LineSegment StartX=-9.8839 StartY=2.24645 StartZ=0 EndX=-7.9084 EndY=2.24645 EndZ=0
    g200: LineSegment StartX=-9.8839 StartY=2.80965 StartZ=0 EndX=-9.8839 EndY=4.78515 EndZ=0
    g201: LineSegment StartX=-7.9084 StartY=2.80965 StartZ=0 EndX=-7.9084 EndY=4.78515 EndZ=0
    g202: LineSegment StartX=-9.8839 StartY=2.80965 StartZ=0 EndX=-7.9084 EndY=2.80965 EndZ=0
    g203: LineSegment StartX=-9.8839 StartY=4.78515 StartZ=0 EndX=-7.9084 EndY=4.78515 EndZ=0
    g204: LineSegment StartX=-9.8839 StartY=5.34835 StartZ=0 EndX=-9.8839 EndY=7.32385 EndZ=0
    g205: LineSegment StartX=-7.9084 StartY=5.34835 StartZ=0 EndX=-7.9084 EndY=7.32385 EndZ=0
    g206: LineSegment StartX=-9.8839 StartY=5.34835 StartZ=0 EndX=-7.9084 EndY=5.34835 EndZ=0
    g207: LineSegment StartX=-9.8839 StartY=7.32385 StartZ=0 EndX=-7.9084 EndY=7.32385 EndZ=0
    g208: LineSegment StartX=-9.8839 StartY=7.88705 StartZ=0 EndX=-9.8839 EndY=9.86255 EndZ=0
    g209: LineSegment StartX=-7.9084 StartY=7.88705 StartZ=0 EndX=-7.9084 EndY=9.86255 EndZ=0
    g210: LineSegment StartX=-9.8839 StartY=7.88705 StartZ=0 EndX=-7.9084 EndY=7.88705 EndZ=0
    g211: LineSegment StartX=-9.8839 StartY=9.86255 StartZ=0 EndX=-7.9084 EndY=9.86255 EndZ=0
    g212: LineSegment StartX=-9.8839 StartY=10.4257 StartZ=0 EndX=-9.8839 EndY=12.4012 EndZ=0
    g213: LineSegment StartX=-7.9084 StartY=10.4257 StartZ=0 EndX=-7.9084 EndY=12.4012 EndZ=0
    g214: LineSegment StartX=-9.8839 StartY=10.4257 StartZ=0 EndX=-7.9084 EndY=10.4257 EndZ=0
    g215: LineSegment StartX=-9.8839 StartY=12.4012 StartZ=0 EndX=-7.9084 EndY=12.4012 EndZ=0
    g216: LineSegment StartX=-9.8839 StartY=12.9644 StartZ=0 EndX=-9.8839 EndY=14.9399 EndZ=0
    g217: LineSegment StartX=-7.9084 StartY=12.9644 StartZ=0 EndX=-7.9084 EndY=14.9399 EndZ=0
    g218: LineSegment StartX=-9.8839 StartY=12.9644 StartZ=0 EndX=-7.9084 EndY=12.9644 EndZ=0
    g219: LineSegment StartX=-9.8839 StartY=14.9399 StartZ=0 EndX=-7.9084 EndY=14.9399 EndZ=0
    g220: LineSegment StartX=-9.8839 StartY=15.5031 StartZ=0 EndX=-9.8839 EndY=17.4786 EndZ=0
    g221: LineSegment StartX=-7.9084 StartY=15.5031 StartZ=0 EndX=-7.9084 EndY=17.4786 EndZ=0
    g222: LineSegment StartX=-9.8839 StartY=15.5031 StartZ=0 EndX=-7.9084 EndY=15.5031 EndZ=0
    g223: LineSegment StartX=-9.8839 StartY=17.4786 StartZ=0 EndX=-7.9084 EndY=17.4786 EndZ=0
    g224: LineSegment StartX=-7.3452 StartY=-17.5 StartZ=0 EndX=-7.3452 EndY=-15.5245 EndZ=0
    g225: LineSegment StartX=-5.3697 StartY=-17.5 StartZ=0 EndX=-5.3697 EndY=-15.5245 EndZ=0
    g226: LineSegment StartX=-7.3452 StartY=-17.5 StartZ=0 EndX=-5.3697 EndY=-17.5 EndZ=0
    g227: LineSegment StartX=-7.3452 StartY=-15.5245 StartZ=0 EndX=-5.3697 EndY=-15.5245 EndZ=0
    g228: LineSegment StartX=-7.3452 StartY=-14.9613 StartZ=0 EndX=-7.3452 EndY=-12.9858 EndZ=0
    g229: LineSegment StartX=-5.3697 StartY=-14.9613 StartZ=0 EndX=-5.3697 EndY=-12.9858 EndZ=0
    g230: LineSegment StartX=-7.3452 StartY=-14.9613 StartZ=0 EndX=-5.3697 EndY=-14.9613 EndZ=0
    g231: LineSegment StartX=-7.3452 StartY=-12.9858 StartZ=0 EndX=-5.3697 EndY=-12.9858 EndZ=0
    g232: LineSegment StartX=-7.3452 StartY=-12.4226 StartZ=0 EndX=-7.3452 EndY=-10.4471 EndZ=0
    g233: LineSegment StartX=-5.3697 StartY=-12.4226 StartZ=0 EndX=-5.3697 EndY=-10.4471 EndZ=0
    g234: LineSegment StartX=-7.3452 StartY=-12.4226 StartZ=0 EndX=-5.3697 EndY=-12.4226 EndZ=0
    g235: LineSegment StartX=-7.3452 StartY=-10.4471 StartZ=0 EndX=-5.3697 EndY=-10.4471 EndZ=0
    g236: LineSegment StartX=-7.3452 StartY=-9.88385 StartZ=0 EndX=-7.3452 EndY=-7.90835 EndZ=0
    g237: LineSegment StartX=-5.3697 StartY=-9.88385 StartZ=0 EndX=-5.3697 EndY=-7.90835 EndZ=0
    g238: LineSegment StartX=-7.3452 StartY=-9.88385 StartZ=0 EndX=-5.3697 EndY=-9.88385 EndZ=0
    g239: LineSegment StartX=-7.3452 StartY=-7.90835 StartZ=0 EndX=-5.3697 EndY=-7.90835 EndZ=0
    g240: LineSegment StartX=-7.3452 StartY=-7.34515 StartZ=0 EndX=-7.3452 EndY=-5.36965 EndZ=0
    g241: LineSegment StartX=-5.3697 StartY=-7.34515 StartZ=0 EndX=-5.3697 EndY=-5.36965 EndZ=0
    g242: LineSegment StartX=-7.3452 StartY=-7.34515 StartZ=0 EndX=-5.3697 EndY=-7.34515 EndZ=0
    g243: LineSegment StartX=-7.3452 StartY=-5.36965 StartZ=0 EndX=-5.3697 EndY=-5.36965 EndZ=0
    g244: LineSegment StartX=-7.3452 StartY=-4.80645 StartZ=0 EndX=-7.3452 EndY=-2.83095 EndZ=0
    g245: LineSegment StartX=-5.3697 StartY=-4.80645 StartZ=0 EndX=-5.3697 EndY=-2.83095 EndZ=0
    g246: LineSegment StartX=-7.3452 StartY=-4.80645 StartZ=0 EndX=-5.3697 EndY=-4.80645 EndZ=0
    g247: LineSegment StartX=-7.3452 StartY=-2.83095 StartZ=0 EndX=-5.3697 EndY=-2.83095 EndZ=0
    g248: LineSegment StartX=-7.3452 StartY=-2.26775 StartZ=0 EndX=-7.3452 EndY=-0.292254 EndZ=0
    g249: LineSegment StartX=-5.3697 StartY=-2.26775 StartZ=0 EndX=-5.3697 EndY=-0.292254 EndZ=0
    g250: LineSegment StartX=-7.3452 StartY=-2.26775 StartZ=0 EndX=-5.3697 EndY=-2.26775 EndZ=0
    g251: LineSegment StartX=-7.3452 StartY=-0.292254 StartZ=0 EndX=-5.3697 EndY=-0.292254 EndZ=0
    g252: LineSegment StartX=-7.3452 StartY=0.270946 StartZ=0 EndX=-7.3452 EndY=2.24645 EndZ=0
    g253: LineSegment StartX=-5.3697 StartY=0.270946 StartZ=0 EndX=-5.3697 EndY=2.24645 EndZ=0
    g254: LineSegment StartX=-7.3452 StartY=0.270946 StartZ=0 EndX=-5.3697 EndY=0.270946 EndZ=0
    g255: LineSegment StartX=-7.3452 StartY=2.24645 StartZ=0 EndX=-5.3697 EndY=2.24645 EndZ=0
    g256: LineSegment StartX=-7.3452 StartY=2.80965 StartZ=0 EndX=-7.3452 EndY=4.78515 EndZ=0
    g257: LineSegment StartX=-5.3697 StartY=2.80965 StartZ=0 EndX=-5.3697 EndY=4.78515 EndZ=0
    g258: LineSegment StartX=-7.3452 StartY=2.80965 StartZ=0 EndX=-5.3697 EndY=2.80965 EndZ=0
    g259: LineSegment StartX=-7.3452 StartY=4.78515 StartZ=0 EndX=-5.3697 EndY=4.78515 EndZ=0
    g260: LineSegment StartX=-7.3452 StartY=5.34835 StartZ=0 EndX=-7.3452 EndY=7.32385 EndZ=0
    g261: LineSegment StartX=-5.3697 StartY=5.34835 StartZ=0 EndX=-5.3697 EndY=7.32385 EndZ=0
    g262: LineSegment StartX=-7.3452 StartY=5.34835 StartZ=0 EndX=-5.3697 EndY=5.34835 EndZ=0
    g263: LineSegment StartX=-7.3452 StartY=7.32385 StartZ=0 EndX=-5.3697 EndY=7.32385 EndZ=0
    g264: LineSegment StartX=-7.3452 StartY=7.88705 StartZ=0 EndX=-7.3452 EndY=9.86255 EndZ=0
    g265: LineSegment StartX=-5.3697 StartY=7.88705 StartZ=0 EndX=-5.3697 EndY=9.86255 EndZ=0
    g266: LineSegment StartX=-7.3452 StartY=7.88705 StartZ=0 EndX=-5.3697 EndY=7.88705 EndZ=0
    g267: LineSegment StartX=-7.3452 StartY=9.86255 StartZ=0 EndX=-5.3697 EndY=9.86255 EndZ=0
    g268: LineSegment StartX=-7.3452 StartY=10.4257 StartZ=0 EndX=-7.3452 EndY=12.4012 EndZ=0
    g269: LineSegment StartX=-5.3697 StartY=10.4257 StartZ=0 EndX=-5.3697 EndY=12.4012 EndZ=0
    g270: LineSegment StartX=-7.3452 StartY=10.4257 StartZ=0 EndX=-5.3697 EndY=10.4257 EndZ=0
    g271: LineSegment StartX=-7.3452 StartY=12.4012 StartZ=0 EndX=-5.3697 EndY=12.4012 EndZ=0
    g272: LineSegment StartX=-7.3452 StartY=12.9644 StartZ=0 EndX=-7.3452 EndY=14.9399 EndZ=0
    g273: LineSegment StartX=-5.3697 StartY=12.9644 StartZ=0 EndX=-5.3697 EndY=14.9399 EndZ=0
    g274: LineSegment StartX=-7.3452 StartY=12.9644 StartZ=0 EndX=-5.3697 EndY=12.9644 EndZ=0
    g275: LineSegment StartX=-7.3452 StartY=14.9399 StartZ=0 EndX=-5.3697 EndY=14.9399 EndZ=0
    g276: LineSegment StartX=-7.3452 StartY=15.5031 StartZ=0 EndX=-7.3452 EndY=17.4786 EndZ=0
    g277: LineSegment StartX=-5.3697 StartY=15.5031 StartZ=0 EndX=-5.3697 EndY=17.4786 EndZ=0
    g278: LineSegment StartX=-7.3452 StartY=15.5031 StartZ=0 EndX=-5.3697 EndY=15.5031 EndZ=0
    g279: LineSegment StartX=-7.3452 StartY=17.4786 StartZ=0 EndX=-5.3697 EndY=17.4786 EndZ=0
    g280: LineSegment StartX=-4.8065 StartY=-17.5 StartZ=0 EndX=-4.8065 EndY=-15.5245 EndZ=0
    g281: LineSegment StartX=-2.831 StartY=-17.5 StartZ=0 EndX=-2.831 EndY=-15.5245 EndZ=0
    g282: LineSegment StartX=-4.8065 StartY=-17.5 StartZ=0 EndX=-2.831 EndY=-17.5 EndZ=0
    g283: LineSegment StartX=-4.8065 StartY=-15.5245 StartZ=0 EndX=-2.831 EndY=-15.5245 EndZ=0
    g284: LineSegment StartX=-4.8065 StartY=-14.9613 StartZ=0 EndX=-4.8065 EndY=-12.9858 EndZ=0
    g285: LineSegment StartX=-2.831 StartY=-14.9613 StartZ=0 EndX=-2.831 EndY=-12.9858 EndZ=0
    g286: LineSegment StartX=-4.8065 StartY=-14.9613 StartZ=0 EndX=-2.831 EndY=-14.9613 EndZ=0
    g287: LineSegment StartX=-4.8065 StartY=-12.9858 StartZ=0 EndX=-2.831 EndY=-12.9858 EndZ=0
    g288: LineSegment StartX=-4.8065 StartY=-12.4226 StartZ=0 EndX=-4.8065 EndY=-10.4471 EndZ=0
    g289: LineSegment StartX=-2.831 StartY=-12.4226 StartZ=0 EndX=-2.831 EndY=-10.4471 EndZ=0
    g290: LineSegment StartX=-4.8065 StartY=-12.4226 StartZ=0 EndX=-2.831 EndY=-12.4226 EndZ=0
    g291: LineSegment StartX=-4.8065 StartY=-10.4471 StartZ=0 EndX=-2.831 EndY=-10.4471 EndZ=0
    g292: LineSegment StartX=-4.8065 StartY=-9.88385 StartZ=0 EndX=-4.8065 EndY=-7.90835 EndZ=0
    g293: LineSegment StartX=-2.831 StartY=-9.88385 StartZ=0 EndX=-2.831 EndY=-7.90835 EndZ=0
    g294: LineSegment StartX=-4.8065 StartY=-9.88385 StartZ=0 EndX=-2.831 EndY=-9.88385 EndZ=0
    g295: LineSegment StartX=-4.8065 StartY=-7.90835 StartZ=0 EndX=-2.831 EndY=-7.90835 EndZ=0
    g296: LineSegment StartX=-4.8065 StartY=-7.34515 StartZ=0 EndX=-4.8065 EndY=-5.36965 EndZ=0
    g297: LineSegment StartX=-2.831 StartY=-7.34515 StartZ=0 EndX=-2.831 EndY=-5.36965 EndZ=0
    g298: LineSegment StartX=-4.8065 StartY=-7.34515 StartZ=0 EndX=-2.831 EndY=-7.34515 EndZ=0
    g299: LineSegment StartX=-4.8065 StartY=-5.36965 StartZ=0 EndX=-2.831 EndY=-5.36965 EndZ=0
    g300: LineSegment StartX=-4.8065 StartY=-4.80645 StartZ=0 EndX=-4.8065 EndY=-2.83095 EndZ=0
    g301: LineSegment StartX=-2.831 StartY=-4.80645 StartZ=0 EndX=-2.831 EndY=-2.83095 EndZ=0
    g302: LineSegment StartX=-4.8065 StartY=-4.80645 StartZ=0 EndX=-2.831 EndY=-4.80645 EndZ=0
    g303: LineSegment StartX=-4.8065 StartY=-2.83095 StartZ=0 EndX=-2.831 EndY=-2.83095 EndZ=0
    g304: LineSegment StartX=-4.8065 StartY=-2.26775 StartZ=0 EndX=-4.8065 EndY=-0.292254 EndZ=0
    g305: LineSegment StartX=-2.831 StartY=-2.26775 StartZ=0 EndX=-2.831 EndY=-0.292254 EndZ=0
    g306: LineSegment StartX=-4.8065 StartY=-2.26775 StartZ=0 EndX=-2.831 EndY=-2.26775 EndZ=0
    g307: LineSegment StartX=-4.8065 StartY=-0.292254 StartZ=0 EndX=-2.831 EndY=-0.292254 EndZ=0
    g308: LineSegment StartX=-4.8065 StartY=0.270946 StartZ=0 EndX=-4.8065 EndY=2.24645 EndZ=0
    g309: LineSegment StartX=-2.831 StartY=0.270946 StartZ=0 EndX=-2.831 EndY=2.24645 EndZ=0
    g310: LineSegment StartX=-4.8065 StartY=0.270946 StartZ=0 EndX=-2.831 EndY=0.270946 EndZ=0
    g311: LineSegment StartX=-4.8065 StartY=2.24645 StartZ=0 EndX=-2.831 EndY=2.24645 EndZ=0
    g312: LineSegment StartX=-4.8065 StartY=2.80965 StartZ=0 EndX=-4.8065 EndY=4.78515 EndZ=0
    g313: LineSegment StartX=-2.831 StartY=2.80965 StartZ=0 EndX=-2.831 EndY=4.78515 EndZ=0
    g314: LineSegment StartX=-4.8065 StartY=2.80965 StartZ=0 EndX=-2.831 EndY=2.80965 EndZ=0
    g315: LineSegment StartX=-4.8065 StartY=4.78515 StartZ=0 EndX=-2.831 EndY=4.78515 EndZ=0
    g316: LineSegment StartX=-4.8065 StartY=5.34835 StartZ=0 EndX=-4.8065 EndY=7.32385 EndZ=0
    g317: LineSegment StartX=-2.831 StartY=5.34835 StartZ=0 EndX=-2.831 EndY=7.32385 EndZ=0
    g318: LineSegment StartX=-4.8065 StartY=5.34835 StartZ=0 EndX=-2.831 EndY=5.34835 EndZ=0
    g319: LineSegment StartX=-4.8065 StartY=7.32385 StartZ=0 EndX=-2.831 EndY=7.32385 EndZ=0
    g320: LineSegment StartX=-4.8065 StartY=7.88705 StartZ=0 EndX=-4.8065 EndY=9.86255 EndZ=0
    g321: LineSegment StartX=-2.831 StartY=7.88705 StartZ=0 EndX=-2.831 EndY=9.86255 EndZ=0
    g322: LineSegment StartX=-4.8065 StartY=7.88705 StartZ=0 EndX=-2.831 EndY=7.88705 EndZ=0
    g323: LineSegment StartX=-4.8065 StartY=9.86255 StartZ=0 EndX=-2.831 EndY=9.86255 EndZ=0
    g324: LineSegment StartX=-4.8065 StartY=10.4257 StartZ=0 EndX=-4.8065 EndY=12.4012 EndZ=0
    g325: LineSegment StartX=-2.831 StartY=10.4257 StartZ=0 EndX=-2.831 EndY=12.4012 EndZ=0
    g326: LineSegment StartX=-4.8065 StartY=10.4257 StartZ=0 EndX=-2.831 EndY=10.4257 EndZ=0
    g327: LineSegment StartX=-4.8065 StartY=12.4012 StartZ=0 EndX=-2.831 EndY=12.4012 EndZ=0
    g328: LineSegment StartX=-4.8065 StartY=12.9644 StartZ=0 EndX=-4.8065 EndY=14.9399 EndZ=0
    g329: LineSegment StartX=-2.831 StartY=12.9644 StartZ=0 EndX=-2.831 EndY=14.9399 EndZ=0
    g330: LineSegment StartX=-4.8065 StartY=12.9644 StartZ=0 EndX=-2.831 EndY=12.9644 EndZ=0
    g331: LineSegment StartX=-4.8065 StartY=14.9399 StartZ=0 EndX=-2.831 EndY=14.9399 EndZ=0
    g332: LineSegment StartX=-4.8065 StartY=15.5031 StartZ=0 EndX=-4.8065 EndY=17.4786 EndZ=0
    g333: LineSegment StartX=-2.831 StartY=15.5031 StartZ=0 EndX=-2.831 EndY=17.4786 EndZ=0
    g334: LineSegment StartX=-4.8065 StartY=15.5031 StartZ=0 EndX=-2.831 EndY=15.5031 EndZ=0
    g335: LineSegment StartX=-4.8065 StartY=17.4786 StartZ=0 EndX=-2.831 EndY=17.4786 EndZ=0
    g336: LineSegment StartX=2.8096 StartY=-17.5 StartZ=0 EndX=2.8096 EndY=-15.5245 EndZ=0
    g337: LineSegment StartX=4.7851 StartY=-17.5 StartZ=0 EndX=4.7851 EndY=-15.5245 EndZ=0
    g338: LineSegment StartX=2.8096 StartY=-17.5 StartZ=0 EndX=4.7851 EndY=-17.5 EndZ=0
    g339: LineSegment StartX=2.8096 StartY=-15.5245 StartZ=0 EndX=4.7851 EndY=-15.5245 EndZ=0
    g340: LineSegment StartX=2.8096 StartY=-14.9613 StartZ=0 EndX=2.8096 EndY=-12.9858 EndZ=0
    g341: LineSegment StartX=4.7851 StartY=-14.9613 StartZ=0 EndX=4.7851 EndY=-12.9858 EndZ=0
    g342: LineSegment StartX=2.8096 StartY=-14.9613 StartZ=0 EndX=4.7851 EndY=-14.9613 EndZ=0
    g343: LineSegment StartX=2.8096 StartY=-12.9858 StartZ=0 EndX=4.7851 EndY=-12.9858 EndZ=0
    g344: LineSegment StartX=2.8096 StartY=-12.4226 StartZ=0 EndX=2.8096 EndY=-10.4471 EndZ=0
    g345: LineSegment StartX=4.7851 StartY=-12.4226 StartZ=0 EndX=4.7851 EndY=-10.4471 EndZ=0
    g346: LineSegment StartX=2.8096 StartY=-12.4226 StartZ=0 EndX=4.7851 EndY=-12.4226 EndZ=0
    g347: LineSegment StartX=2.8096 StartY=-10.4471 StartZ=0 EndX=4.7851 EndY=-10.4471 EndZ=0
    g348: LineSegment StartX=2.8096 StartY=-9.88385 StartZ=0 EndX=2.8096 EndY=-7.90835 EndZ=0
    g349: LineSegment StartX=4.7851 StartY=-9.88385 StartZ=0 EndX=4.7851 EndY=-7.90835 EndZ=0
    g350: LineSegment StartX=2.8096 StartY=-9.88385 StartZ=0 EndX=4.7851 EndY=-9.88385 EndZ=0
    g351: LineSegment StartX=2.8096 StartY=-7.90835 StartZ=0 EndX=4.7851 EndY=-7.90835 EndZ=0
    g352: LineSegment StartX=2.8096 StartY=-7.34515 StartZ=0 EndX=2.8096 EndY=-5.36965 EndZ=0
    g353: LineSegment StartX=4.7851 StartY=-7.34515 StartZ=0 EndX=4.7851 EndY=-5.36965 EndZ=0
    g354: LineSegment StartX=2.8096 StartY=-7.34515 StartZ=0 EndX=4.7851 EndY=-7.34515 EndZ=0
    g355: LineSegment StartX=2.8096 StartY=-5.36965 StartZ=0 EndX=4.7851 EndY=-5.36965 EndZ=0
    g356: LineSegment StartX=2.8096 StartY=-4.80645 StartZ=0 EndX=2.8096 EndY=-2.83095 EndZ=0
    g357: LineSegment StartX=4.7851 StartY=-4.80645 StartZ=0 EndX=4.7851 EndY=-2.83095 EndZ=0
    g358: LineSegment StartX=2.8096 StartY=-4.80645 StartZ=0 EndX=4.7851 EndY=-4.80645 EndZ=0
    g359: LineSegment StartX=2.8096 StartY=-2.83095 StartZ=0 EndX=4.7851 EndY=-2.83095 EndZ=0
    g360: LineSegment StartX=2.8096 StartY=-2.26775 StartZ=0 EndX=2.8096 EndY=-0.292254 EndZ=0
    g361: LineSegment StartX=4.7851 StartY=-2.26775 StartZ=0 EndX=4.7851 EndY=-0.292254 EndZ=0
    g362: LineSegment StartX=2.8096 StartY=-2.26775 StartZ=0 EndX=4.7851 EndY=-2.26775 EndZ=0
    g363: LineSegment StartX=2.8096 StartY=-0.292254 StartZ=0 EndX=4.7851 EndY=-0.292254 EndZ=0
    g364: LineSegment StartX=2.8096 StartY=0.270946 StartZ=0 EndX=2.8096 EndY=2.24645 EndZ=0
    g365: LineSegment StartX=4.7851 StartY=0.270946 StartZ=0 EndX=4.7851 EndY=2.24645 EndZ=0
    g366: LineSegment StartX=2.8096 StartY=0.270946 StartZ=0 EndX=4.7851 EndY=0.270946 EndZ=0
    g367: LineSegment StartX=2.8096 StartY=2.24645 StartZ=0 EndX=4.7851 EndY=2.24645 EndZ=0
    g368: LineSegment StartX=2.8096 StartY=2.80965 StartZ=0 EndX=2.8096 EndY=4.78515 EndZ=0
    g369: LineSegment StartX=4.7851 StartY=2.80965 StartZ=0 EndX=4.7851 EndY=4.78515 EndZ=0
    g370: LineSegment StartX=2.8096 StartY=2.80965 StartZ=0 EndX=4.7851 EndY=2.80965 EndZ=0
    g371: LineSegment StartX=2.8096 StartY=4.78515 StartZ=0 EndX=4.7851 EndY=4.78515 EndZ=0
    g372: LineSegment StartX=2.8096 StartY=5.34835 StartZ=0 EndX=2.8096 EndY=7.32385 EndZ=0
    g373: LineSegment StartX=4.7851 StartY=5.34835 StartZ=0 EndX=4.7851 EndY=7.32385 EndZ=0
    g374: LineSegment StartX=2.8096 StartY=5.34835 StartZ=0 EndX=4.7851 EndY=5.34835 EndZ=0
    g375: LineSegment StartX=2.8096 StartY=7.32385 StartZ=0 EndX=4.7851 EndY=7.32385 EndZ=0
    g376: LineSegment StartX=2.8096 StartY=7.88705 StartZ=0 EndX=2.8096 EndY=9.86255 EndZ=0
    g377: LineSegment StartX=4.7851 StartY=7.88705 StartZ=0 EndX=4.7851 EndY=9.86255 EndZ=0
    g378: LineSegment StartX=2.8096 StartY=7.88705 StartZ=0 EndX=4.7851 EndY=7.88705 EndZ=0
    g379: LineSegment StartX=2.8096 StartY=9.86255 StartZ=0 EndX=4.7851 EndY=9.86255 EndZ=0
    g380: LineSegment StartX=2.8096 StartY=10.4257 StartZ=0 EndX=2.8096 EndY=12.4012 EndZ=0
    g381: LineSegment StartX=4.7851 StartY=10.4257 StartZ=0 EndX=4.7851 EndY=12.4012 EndZ=0
    g382: LineSegment StartX=2.8096 StartY=10.4257 StartZ=0 EndX=4.7851 EndY=10.4257 EndZ=0
    g383: LineSegment StartX=2.8096 StartY=12.4012 StartZ=0 EndX=4.7851 EndY=12.4012 EndZ=0
    g384: LineSegment StartX=2.8096 StartY=12.9644 StartZ=0 EndX=2.8096 EndY=14.9399 EndZ=0
    g385: LineSegment StartX=4.7851 StartY=12.9644 StartZ=0 EndX=4.7851 EndY=14.9399 EndZ=0
    g386: LineSegment StartX=2.8096 StartY=12.9644 StartZ=0 EndX=4.7851 EndY=12.9644 EndZ=0
    g387: LineSegment StartX=2.8096 StartY=14.9399 StartZ=0 EndX=4.7851 EndY=14.9399 EndZ=0
    g388: LineSegment StartX=2.8096 StartY=15.5031 StartZ=0 EndX=2.8096 EndY=17.4786 EndZ=0
    g389: LineSegment StartX=4.7851 StartY=15.5031 StartZ=0 EndX=4.7851 EndY=17.4786 EndZ=0
    g390: LineSegment StartX=2.8096 StartY=15.5031 StartZ=0 EndX=4.7851 EndY=15.5031 EndZ=0
    g391: LineSegment StartX=2.8096 StartY=17.4786 StartZ=0 EndX=4.7851 EndY=17.4786 EndZ=0
    g392: LineSegment StartX=5.3483 StartY=-17.5 StartZ=0 EndX=5.3483 EndY=-15.5245 EndZ=0
    g393: LineSegment StartX=7.3238 StartY=-17.5 StartZ=0 EndX=7.3238 EndY=-15.5245 EndZ=0
    g394: LineSegment StartX=5.3483 StartY=-17.5 StartZ=0 EndX=7.3238 EndY=-17.5 EndZ=0
    g395: LineSegment StartX=5.3483 StartY=-15.5245 StartZ=0 EndX=7.3238 EndY=-15.5245 EndZ=0
    g396: LineSegment StartX=5.3483 StartY=-14.9613 StartZ=0 EndX=5.3483 EndY=-12.9858 EndZ=0
    g397: LineSegment StartX=7.3238 StartY=-14.9613 StartZ=0 EndX=7.3238 EndY=-12.9858 EndZ=0
    g398: LineSegment StartX=5.3483 StartY=-14.9613 StartZ=0 EndX=7.3238 EndY=-14.9613 EndZ=0
    g399: LineSegment StartX=5.3483 StartY=-12.9858 StartZ=0 EndX=7.3238 EndY=-12.9858 EndZ=0
    ... +272 more geometry lines
FEATURE [PartDesign::Pad] Pad
  BaseFeature = -> Box
  Direction = (0,0,1)
  Length = 18
  Length2 = 10
  Placement = pos=(-17.5,-17.5,0) rot=(0,0,1;0rad)
  Profile = -> Sketch001
  ReferenceAxis = -> Sketch001 [N_Axis]
  Type = 0
FEATURE [PartDesign::AdditiveBox] Box013
  AttacherType = Attacher::AttachEngine3D
  AttachmentOffset = pos=(22.5,-15,2.5) rot=(0,0,1;0rad)
  BaseFeature = -> Fillet002
  Height = 2
  Length = 3
  MapMode = 5
  Placement = pos=(22.5,-15,2.5) rot=(0,0,1;0rad)
  Support = -> [XY_Plane001]
  Width = 8
FEATURE [PartDesign::Chamfer] Chamfer
  Angle = 50
  Base = -> Box013 [Edge23,Edge39]
  BaseFeature = -> Box013
  ChamferType = 2
  FlipDirection = false
  Placement = pos=(22.5,-15,2.5) rot=(0,0,1;0rad)
  Size = 0.499
  Size2 = 1
  SupportTransform = false
  UseAllEdges = false
FEATURE [PartDesign::Fillet] Fillet008
  Base = -> Pad [Edge116,Edge124,Edge132,Edge140,Edge184,Edge192,Edge200,Edge412,Edge420,Edge428,Edge484,Edge492,Edge500,Edge508,Edge206,Edge210,Edge230,Edge234,Edge302,Edge314,Edge318,Edge514,Edge518,Edge538,Edge586,Edge590,Edge610,Edge614]
  BaseFeature = -> Pad
  Placement = pos=(-17.5,-17.5,0) rot=(0,0,1;0rad)
  Radius = 2.82
  SupportTransform = false
  UseAllEdges = false
FEATURE [PartDesign::Body] Body  label="Main"
  Group = -> [Box,Sketch001,Pad,Fillet008]
  Origin = -> Origin
  Placement = pos=(0,0,0.05) rot=(0,0,1;1.5708rad)
  Tip = -> Fillet008
FEATURE [PartDesign::Body] Body003  label="metal-film"
  Group = -> [Box016]
  Origin = -> Origin004
  Tip = -> Box016
FEATURE [PartDesign::Chamfer] Chamfer001
  Angle = 40
  Base = -> Chamfer [Edge85,Edge26]
  BaseFeature = -> Chamfer
  ChamferType = 2
  FlipDirection = false
  Placement = pos=(22.5,-15,2.5) rot=(0,0,1;0rad)
  Size = 0.5955
  Size2 = 1
  SupportTransform = false
  UseAllEdges = false
FEATURE [PartDesign::Body] Body001  label="spring-arms"
  Group = -> [Box010,Box011,Box012,Fillet,Fillet001,Fillet002,Box013,Chamfer,Chamfer001]
  Origin = -> Origin001
  Placement = pos=(0,-0.55,0) rot=(0,0,1;0rad)
  Tip = -> Chamfer001
FEATURE [PartDesign::Body] Body002  label="plastic-clamp"
  Group = -> [Box014,Box015]
  Origin = -> Origin002
  Placement = pos=(0,-0.7,0) rot=(0,0,1;0rad)
  Tip = -> Box015
FEATURE [App::Part] Part  label="Aavid_374724B60024G"
  Group = -> [Body002,Body001,Body,Body003,Shape2DView,Array]
  Origin = -> Origin003
